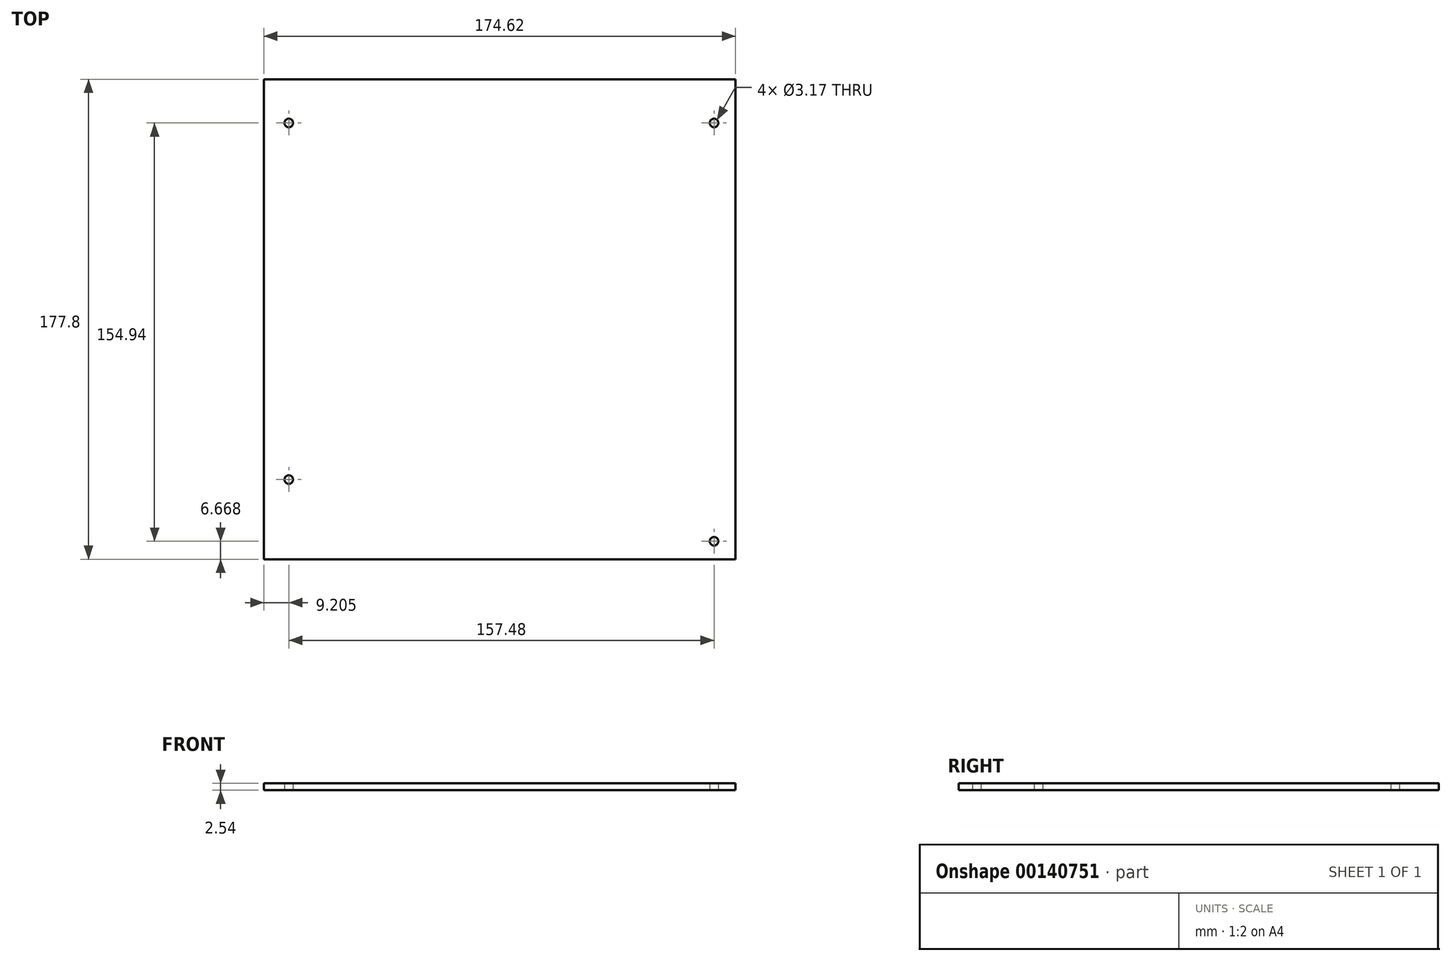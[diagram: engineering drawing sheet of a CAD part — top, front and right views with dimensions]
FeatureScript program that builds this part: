
annotation { "Feature Type Name" : "Feature", "Feature Type Description" : "" }
export const myFeature = defineFeature(function(context is Context, id is Id, definition is map)
    precondition{}
    {
        {
            var Q0;
            Q0=qCreatedBy(makeId("Top.planeOp"),FACE);
            var sketch = newSketch(context, id + "F0", { "sketchPlane" : qUnion([Q0])});
            skLineSegment(sketch, "E0.bottom", {"start": v(87.31, 88.9) * mm, "end": v(-87.31, 88.9) * mm});
            skLineSegment(sketch, "E0.top", {"start": v(87.31, -88.9) * mm, "end": v(-87.31, -88.9) * mm});
            skLineSegment(sketch, "E0.left", {"start": v(87.31, 88.9) * mm, "end": v(87.31, -88.9) * mm});
            skLineSegment(sketch, "E0.right", {"start": v(-87.31, 88.9) * mm, "end": v(-87.31, -88.9) * mm});
            skPoint(sketch, "E0.middle", {"position": v(0, 0) * mm});
            skCircle(sketch, "E1", {"center": v(-78.1, 72.7) * mm, "radius": 1.59 * mm});
            skCircle(sketch, "E2", {"center": v(-78.1, -59.37) * mm, "radius": 1.59 * mm});
            skLineSegment(sketch, "E3.bottom", {"start": v(-88.9, -93.66) * mm, "end": v(88.9, -93.66) * mm, "construction": true});
            skLineSegment(sketch, "E3.top", {"start": v(-88.9, 93.66) * mm, "end": v(88.9, 93.66) * mm, "construction": true});
            skLineSegment(sketch, "E3.left", {"start": v(-88.9, -93.66) * mm, "end": v(-88.9, 93.66) * mm, "construction": true});
            skLineSegment(sketch, "E3.right", {"start": v(88.9, -93.66) * mm, "end": v(88.9, 93.66) * mm, "construction": true});
            skCircle(sketch, "E4", {"center": v(79.37, 72.7) * mm, "radius": 1.59 * mm});
            skCircle(sketch, "E5", {"center": v(79.37, -82.23) * mm, "radius": 1.59 * mm});
            skSolve(sketch);
        }
        {
            var Q0;
            Q0 = qSketchRegion(id + "F0", true);
            extrude(context, id + "F1", {"entities" : qUnion([Q0]), "depth" : 2.54 * mm});
        }
    });
